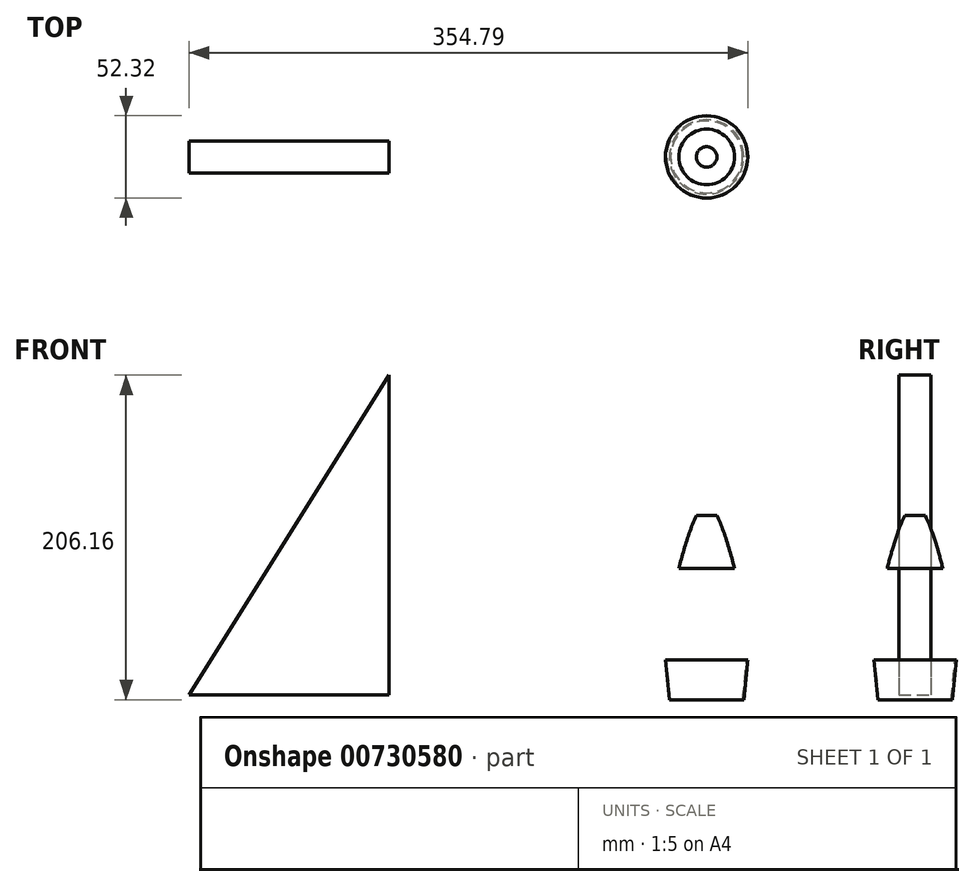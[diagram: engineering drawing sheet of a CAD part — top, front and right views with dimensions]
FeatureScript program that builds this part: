
annotation { "Feature Type Name" : "Feature", "Feature Type Description" : "" }
export const myFeature = defineFeature(function(context is Context, id is Id, definition is map)
    precondition{}
    {
        {
            var Q0;
            Q0=qCreatedBy(makeId("Front.planeOp"),FACE);
            var sketch = newSketch(context, id + "F0", { "sketchPlane" : qUnion([Q0])});
            skLineSegment(sketch, "E0", {"start": v(25.4, 0) * mm, "end": v(26.16, 0) * mm});
            skLineSegment(sketch, "E1", {"start": v(23.62, -25.4) * mm, "end": v(26.16, 0) * mm});
            skFitSpline(sketch, "E2", {"points": [v(26.16, 0) * mm, v(0, 101.92) * mm], "startDerivative": vector(-3.23, 103.51) * mm, "endDerivative": vector(-37.71, 38.93) * mm});
            skFitSpline(sketch, "E3.0", {"points": [v(25.9, 0) * mm, v(25.64, 8.6) * mm, v(23.67, 28.33) * mm, v(18.53, 54.43) * mm, v(13.34, 73.28) * mm, v(9.05, 85.69) * mm, v(4.49, 95.64) * mm, v(1.37, 100.15) * mm, v(-0.18, 101.74) * mm]});
            skLineSegment(sketch, "E4.0", {"start": v(22.86, -25.32) * mm, "end": v(25.4, 0) * mm});
            skLineSegment(sketch, "E5", {"start": v(0, 101.92) * mm, "end": v(0, 101.55) * mm});
            skLineSegment(sketch, "E6", {"start": v(0, 101.55) * mm, "end": v(0, 101.55) * mm});
            skLineSegment(sketch, "E7", {"start": v(22.86, -25.32) * mm, "end": v(23.62, -25.4) * mm});
            skLineSegment(sketch, "E8", {"start": v(0, 0) * mm, "end": v(25.9, 0) * mm});
            skLineSegment(sketch, "E9.0", {"start": v(0, -0.25) * mm, "end": v(25.37, -0.25) * mm});
            skLineSegment(sketch, "E10", {"start": v(0, 0) * mm, "end": v(0, -0.25) * mm});
            skLineSegment(sketch, "E11", {"start": v(0, 101.92) * mm, "end": v(0, -35.08) * mm});
            skSolve(sketch);
        }
        {
            var Q0;
            Q0=qCreatedBy(makeId("Front.planeOp"),FACE);
            var sketch = newSketch(context, id + "F1", { "sketchPlane" : qUnion([Q0])});
            skLineSegment(sketch, "E12.bottom", {"start": v(-201.63, 180.76) * mm, "end": v(-328.63, 180.76) * mm});
            skLineSegment(sketch, "E12.top", {"start": v(-201.63, -22.44) * mm, "end": v(-328.63, -22.44) * mm});
            skLineSegment(sketch, "E12.left", {"start": v(-201.63, 180.76) * mm, "end": v(-201.63, -22.44) * mm});
            skLineSegment(sketch, "E12.right", {"start": v(-328.63, 180.76) * mm, "end": v(-328.63, -22.44) * mm});
            skLineSegment(sketch, "E13", {"start": v(-201.63, 180.76) * mm, "end": v(-328.63, -22.44) * mm});
            skSolve(sketch);
        }
        {
            var Q0;
            Q0=makeQuery(id+"F1.imprint","IMPRINT",FACE,{"disambiguationData":[TD([[makeQuery(id+"F1.imprint","IMPRINT",EDGE,{"derivedFrom":sQuery(id+"F1.wireOp",EDGE,"E12.top")}),-1.0]])]});
            extrude(context, id + "F2", {"entities" : qUnion([Q0]), "depth" : 20.32 * mm, "offsetDistance" : 25.4 * mm, "symmetric" : true});
        }
        {
            var Q0;
            {var subQ0=sQuery(id+"F0.wireOp",EDGE,"E1");Q0=makeQuery(id+"F0.imprint","IMPRINT",FACE,{"disambiguationData":[TD([[makeQuery(id+"F0.imprint","IMPRINT",EDGE,{"derivedFrom":subQ0}),1.0]])]});}
            var Q1;
            {var subQ0=sQuery(id+"F0.wireOp",EDGE,"E8");Q1=makeQuery(id+"F0.imprint","IMPRINT",FACE,{"disambiguationData":[TD([[makeQuery(id+"F0.imprint","IMPRINT",EDGE,{"derivedFrom":subQ0}),-1.0]])]});}
            var Q2;
            {var subQ0=sQuery(id+"F0.wireOp",EDGE,"E2");Q2=makeQuery(id+"F0.imprint","IMPRINT",FACE,{"disambiguationData":[TD([[makeQuery(id+"F0.imprint","IMPRINT",EDGE,{"derivedFrom":subQ0}),1.0]])]});}
            var Q3;
            Q3=sQuery(id+"F0.wireOp",EDGE,"E11");
            revolve(context, id + "F3", {"surfaceOperationType" : NewSurfaceOperationType.NEW, "entities" : qUnion([Q0, Q1, Q2]), "axis" : qUnion([Q3]), "revolveType" : RevolveType.FULL});
        }
    });
